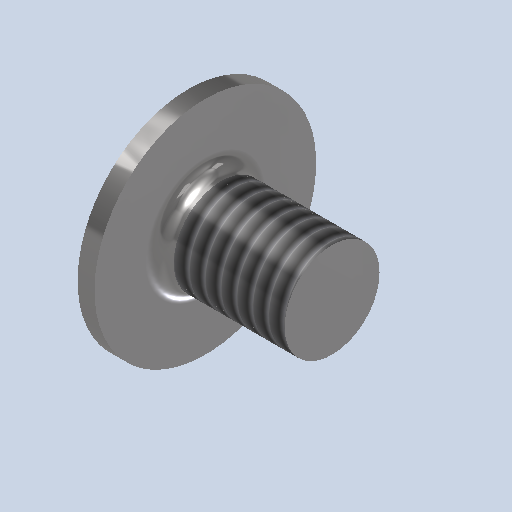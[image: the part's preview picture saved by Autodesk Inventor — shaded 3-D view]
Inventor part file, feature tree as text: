
AUTODESK INVENTOR PART (.ipt)
format: ipt  version: 2022 (Build 260153000, 153)  size: 289,280 bytes
history: native  units: mm
features: sketch x5, extrude x4, revolve x2, projected_geometry x2, thread x1
ambient origin geometry x8: Origin, YZ Plane, XZ Plane, XY Plane, X Axis, Y Axis, Z Axis, Center Point
bodies: Solid1 (feature_tree)
feature tree (14):
  revolve  "Revolution1"  [1 undecoded]
  thread  "Thread1"  [1 undecoded]
  extrude  "Extrusion1"  Depth=6.0mm
  revolve  "Revolution2"  [1 undecoded]
  extrude  "押し出し2"  Depth=0.8mm TaperAngle=0.0deg
  sketch  "スケッチ5"
  extrude  "押し出し3"  [1 undecoded]
  extrude  "押し出し4"  [1 undecoded]
  sketch  "Sketch_1"  dims[d0=360.0deg d1=5.5mm d2=0.1mm d3=0.75mm d4=0.0mm]
  sketch  "Sketch_5"  dims[d7=2.0mm d8=0.0mm d9=0.75mm d10=0.0mm d11=0.8mm d12=0.0mm]
  sketch  "Sketch_2"  dims[d5=360.0deg d6=6.0mm]
  sketch  "スケッチ4"
  projected_geometry  "投影ループ1"
  projected_geometry  "投影ループ2"
note: 5 required parameter values undecoded (feature->parameter linkage not recoverable at this tier; creation-order binding heuristic only, values carry confidence <= 0.55)